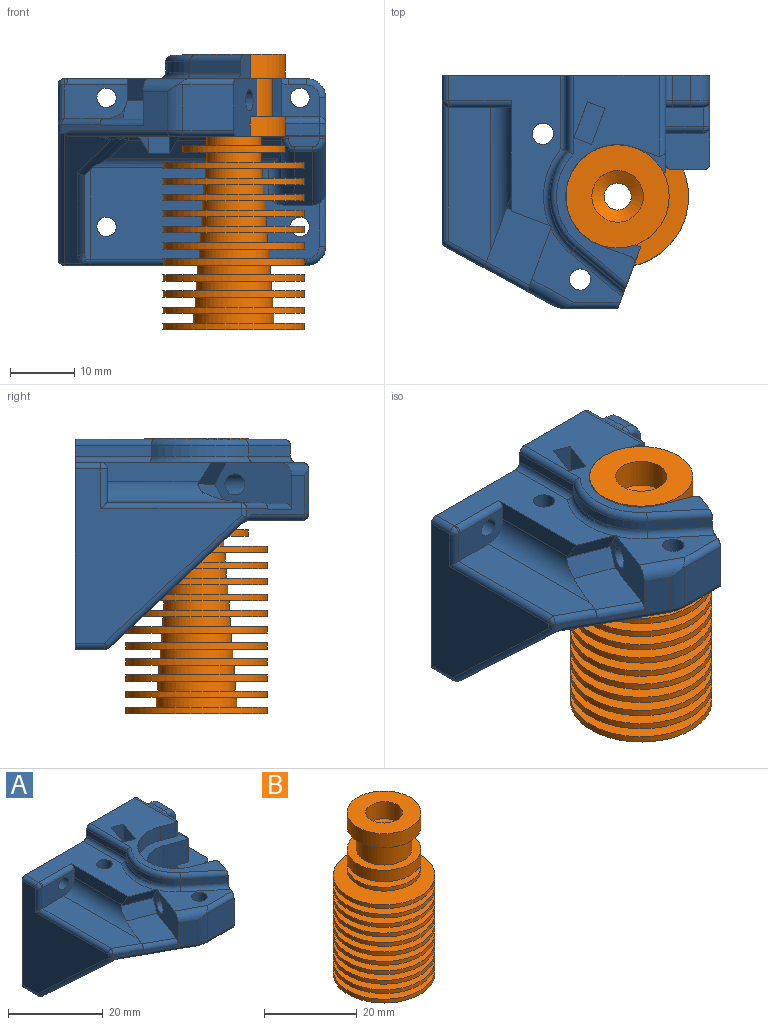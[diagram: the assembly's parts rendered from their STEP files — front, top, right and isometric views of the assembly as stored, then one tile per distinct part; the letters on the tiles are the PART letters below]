
ASSEMBLY  parts=2 mates=1
PART A: 143 faces, bbox 44.2x39.5x35.3 mm
  f0: plane 12.05x7.5mm, normal (-0.94,0.35,0), area 65.9mm2, adj f2,f6,f12,f24,f29,f71,f78,f128
  f1: plane 10.45x3.97mm, normal (0.94,-0.35,0), area 4.8mm2, adj f24,f78,f80,f121,f126,f128,f133
  f2: plane 7x4.48mm, normal (-0.3,-0.81,-0.5), area 27.6mm2, adj f0,f11,f71,f79,f80,f133
  f3: cylinder r=1mm len=12.2mm, axis (0,1,0), area 18.9mm2, adj f14,f15,f28,f72
  f4: cylinder r=1mm len=8.71mm, axis (-0.77,0.64,0), area 16.2mm2, adj f12,f71,f111,f112
  f5: cylinder r=1mm len=11.8mm, axis (0,-1,0), area 18.2mm2, adj f11,f14,f15,f71
  f6: cylinder r=2mm len=7.47mm, axis (0.88,-0.48,0), area 19.6mm2, adj f0,f7,f12,f24,f119
  f7: cylinder r=1mm len=8.72mm, axis (1,0,0), area 12.3mm2, adj f6,f12,f25,f26,f119
  f8: plane 5.92x5.33mm, normal (-0.35,-0.94,0), area 33.7mm2, adj f12,f27,f43,f114
  f9: plane 3.6x3.28mm, normal (-0.35,-0.94,0), area 12.6mm2, adj f12,f28,f98,f132
  f10: plane 5.92x5.74mm, normal (0.35,0.94,0), area 36.3mm2, adj f12,f26,f27,f114
  f11: plane 23.31x17.38mm, normal (0,0,1), area 178.3mm2, adj f2,f5,f14,f55,f56,f71,f79,f90
  f12: plane 24.46x20.78mm, normal (0,0,1), area 131.4mm2, adj f0,f4,f6,f7,f8,f9,f10,f26
  f13: plane 3.97x2.83mm, normal (0,0,1), area 11.2mm2, adj f14,f49,f68,f70
  f14: plane 41.5x32.61mm, normal (0,1,0), area 1226.5mm2, adj f3,f5,f11,f13,f15,f22,f23,f28
  f15: plane 11.8x1.6mm, normal (-1,0,0), area 18.9mm2, adj f3,f5,f14,f113
  f16: cylinder r=2mm len=6.18mm, axis (-0.58,0.58,-0.58), area 14mm2, adj f17,f63,f102,f103,f129,f131
  f17: sphere r=2mm, area 1.2mm2, adj f16,f18,f19
  f18: cylinder r=2mm len=2.07mm, axis (-1,0,0), area 2.9mm2, adj f17,f94,f95,f102,f137
  f19: cylinder r=2mm len=14.49mm, axis (0,-1,0), area 22.8mm2, adj f17,f20,f103,f137
  f20: bspline ~5.62x2.83mm, area 6.8mm2, adj f19,f39,f62,f137
  f21: plane 5.83x5.23mm, normal (0,-1,0), area 21.1mm2, adj f43,f47,f48,f49,f50,f82,f107
  f22: cylinder r=1.5mm len=4.97mm, axis (0,-1,0), area 46.9mm2, adj f14,f131
  f23: cylinder r=1.5mm len=4.97mm, axis (0,-1,0), area 46.9mm2, adj f14,f131
  f24: plane 16.48x9.06mm, normal (-0.48,-0.88,0), area 36.7mm2, adj f0,f1,f6,f39,f78,f119,f122,f123
  f25: plane 7.87x7mm, normal (0,-1,0), area 55.1mm2, adj f7,f26,f119,f142
  f26: plane 9.75x9.16mm, normal (0.94,-0.35,0), area 74mm2, adj f7,f10,f12,f25,f29,f99,f114,f137
  f27: cylinder r=6.05mm len=11.71mm, axis (0,0,1), area 112.5mm2, adj f8,f10,f12,f114
  f28: plane 32.38x15.96mm, normal (0,0,1), area 181.3mm2, adj f3,f9,f14,f72,f73,f98,f101,f104
  f29: cylinder r=1.65mm len=14.34mm, axis (0.94,-0.35,0), area 145.9mm2, adj f0,f26
  f30: cylinder r=2mm len=11.35mm, axis (0,0.75,-0.66), area 39.8mm2, adj f31,f40,f44,f74,f131
  f31: bspline ~2.09x2mm, area 3mm2, adj f30,f51,f52,f76
  f32: bspline ~2.09x2mm, area 3mm2, adj f33,f52,f66,f76
  f33: cylinder r=1mm len=1mm, axis (0,0,1), area 0.6mm2, adj f32,f75,f76,f77
  f34: cylinder r=1mm len=1.95mm, axis (0,0,-1), area 3.1mm2, adj f35,f40,f77,f81
  f35: sphere r=1mm, area 1mm2, adj f34,f36,f37
  f36: cylinder r=1mm len=4mm, axis (0,-1,0), area 5.5mm2, adj f35,f40,f47,f82
  f37: cylinder r=1mm len=5.83mm, axis (-1,0,0), area 9.2mm2, adj f35,f43,f81,f82
  f38: bspline ~2.04x1.4mm, area 2.2mm2, adj f39,f60,f127,f129
  f39: plane 22.71x21.32mm, normal (0,-0.68,-0.73), area 80.7mm2, adj f20,f24,f38,f59,f62,f122,f127,f137
  f40: plane 23.01x13.67mm, normal (1,0,0), area 144.3mm2, adj f14,f30,f34,f36,f44,f47,f51,f68
  f41: plane 37.5x4.58mm, normal (0,0,-1), area 150.8mm2, adj f14,f46,f57,f59,f61,f69
  f42: plane 27.01x25.74mm, normal (-1,0,0), area 350.5mm2, adj f14,f53,f56,f57,f122,f123,f124
  f43: plane 17.63x14mm, normal (1,0,0), area 84.9mm2, adj f8,f12,f14,f21,f37,f50,f70,f77
  f44: cylinder r=1mm len=8.17mm, axis (0,0,-1), area 11.7mm2, adj f30,f40,f45,f131
  f45: torus R=2mm, axis (0,-1,0), area 6.5mm2, adj f44,f46,f69,f131
  f46: cylinder r=1mm len=33.5mm, axis (-1,0,0), area 52.6mm2, adj f41,f45,f61,f131
  f47: cylinder r=1mm len=3.96mm, axis (0,0,-1), area 5.4mm2, adj f21,f36,f40,f48
  f48: torus R=2mm, axis (0,-1,0), area 6.5mm2, adj f21,f47,f49,f68
  f49: cylinder r=1mm len=2.83mm, axis (1,0,0), area 4.4mm2, adj f13,f21,f48,f50
  f50: torus R=2mm, axis (0,-1,0), area 2.1mm2, adj f21,f43,f49,f70
  f51: cylinder r=1mm len=1mm, axis (0,0,1), area 0.6mm2, adj f31,f40,f76,f77
  f52: cylinder r=1mm len=2.83mm, axis (-1,0,0), area 2.4mm2, adj f31,f32,f74,f76
  f53: cylinder r=1mm len=6.2mm, axis (0,0,1), area 9mm2, adj f42,f54,f120,f124
  f54: sphere r=1mm, area 2.1mm2, adj f53,f55,f56
  f55: cylinder r=1mm len=9.7mm, axis (1,0,0), area 15.2mm2, adj f11,f54,f79,f120
  f56: cylinder r=1mm len=3.97mm, axis (0,1,0), area 6.2mm2, adj f11,f14,f42,f54
  f57: cylinder r=1mm len=4.58mm, axis (0,1,0), area 7.2mm2, adj f14,f41,f42,f58
  f58: sphere r=1mm, area 0.8mm2, adj f57,f59,f122
  f59: cylinder r=1mm len=2.57mm, axis (1,0,0), area 1.9mm2, adj f39,f41,f58,f60
  f60: sphere r=1mm, area 0.2mm2, adj f38,f59,f61
  f61: torus R=2mm, axis (0,0,1), area 1.7mm2, adj f41,f46,f60,f129
  f62: cylinder r=2mm len=7.24mm, axis (0.56,-0.6,0.56), area 19.1mm2, adj f20,f39,f103,f127
  f63: cylinder r=2mm len=28.81mm, axis (-1,0,0), area 42mm2, adj f16,f64,f102,f131
  f64: cylinder r=2mm len=7.73mm, axis (0,0,-1), area 14.3mm2, adj f63,f67,f75,f102,f131
  f65: cylinder r=2mm len=16.25mm, axis (-1,0,0), area 25.2mm2, adj f75,f91,f92,f102,f137
  f66: cylinder r=2mm len=8.02mm, axis (0,-0.75,0.66), area 26.7mm2, adj f32,f67,f74,f75
  f67: bspline ~5.03x4.04mm, area 11.8mm2, adj f64,f66,f74,f131
  f68: cylinder r=3mm len=3.97mm, axis (0,1,0), area 18.7mm2, adj f13,f14,f40,f48
  f69: cylinder r=3mm len=3.97mm, axis (0,1,0), area 18.7mm2, adj f14,f40,f41,f45
  f70: cylinder r=1mm len=3.97mm, axis (0,1,0), area 6.2mm2, adj f13,f14,f43,f50
  f71: torus R=11.5mm, axis (0,0,-1), area 27mm2, adj f0,f2,f4,f5,f11,f12,f113
  f72: torus R=9.5mm, axis (0,0,1), area 25.9mm2, adj f3,f28,f73,f113
  f73: cylinder r=1mm len=8.44mm, axis (-0.77,0.64,0), area 15.7mm2, adj f28,f72,f111,f112
  f74: plane 9.36x8.27mm, normal (0,-0.66,-0.75), area 37.7mm2, adj f30,f52,f66,f67,f131
  f75: plane 6.7x6.28mm, normal (-1,0,0), area 19.8mm2, adj f33,f64,f65,f66,f77,f100,f102,f137
  f76: plane 4.83x1.69mm, normal (0,-1,0), area 7.6mm2, adj f31,f32,f33,f51,f52,f77
  f77: plane 6.83x6.7mm, normal (0,0,1), area 38.7mm2, adj f33,f34,f40,f43,f51,f75,f76,f81
  f78: cylinder r=1mm len=7.29mm, axis (-0.88,0.48,0), area 12mm2, adj f0,f1,f24,f128
  f79: plane 17.11x3mm, normal (-1,0,0), area 45.8mm2, adj f2,f11,f55,f80,f120
  f80: cylinder r=3.2mm len=22.24mm, axis (0,-1,0), area 84.9mm2, adj f1,f2,f79,f120,f121,f133
  f81: plane 5.83x1.95mm, normal (0,-1,0), area 11.4mm2, adj f34,f37,f43,f77
  f82: plane 5.83x3mm, normal (0,0,1), area 17.5mm2, adj f21,f36,f37,f43
  f83: plane 2.75x2mm, normal (0.87,0.5,0), area 6.4mm2, adj f84,f88,f89,f137
  f84: plane 3.18x2mm, normal (0,1,0), area 6.4mm2, adj f83,f85,f89,f137
  f85: plane 2.75x2mm, normal (-0.87,0.5,0), area 6.4mm2, adj f84,f86,f89,f137
  f86: plane 2.75x2mm, normal (-0.87,-0.5,0), area 6.4mm2, adj f85,f87,f89,f137
  f87: plane 3.18x2mm, normal (0,-1,0), area 6.4mm2, adj f86,f88,f89,f137
  f88: plane 2.75x2mm, normal (0.87,-0.5,0), area 6.4mm2, adj f83,f87,f89,f137
  f89: plane 6.35x5.5mm, normal (0,0,-1), area 17.6mm2, adj f83,f84,f85,f86,f87,f88,f118
  f90: cylinder r=1.65mm len=7mm, axis (0,0,1), area 72.6mm2, adj f11,f97
  f91: plane 2.76x2.13mm, normal (-0.87,0.5,0), area 6.4mm2, adj f65,f92,f96,f97,f137
  f92: plane 4.65x2.78mm, normal (-0.87,-0.5,0), area 10.4mm2, adj f65,f91,f93,f97,f102
  f93: plane 4.62x3.18mm, normal (0,-1,0), area 14.7mm2, adj f92,f94,f97,f102
  f94: plane 4.65x2.78mm, normal (0.87,-0.5,0), area 10.4mm2, adj f18,f93,f95,f97,f102
  f95: plane 2.76x2.13mm, normal (0.87,0.5,0), area 6.4mm2, adj f18,f94,f96,f97,f137
  f96: plane 3.18x2mm, normal (0,1,0), area 6.4mm2, adj f91,f95,f97,f137
  f97: plane 6.35x5.5mm, normal (0,0,-1), area 17.6mm2, adj f90,f91,f92,f93,f94,f95,f96
  f98: cylinder r=1mm len=3.6mm, axis (0,0,-1), area 6.4mm2, adj f9,f12,f28,f43,f138
  f99: cylinder r=1mm len=3.08mm, axis (0,0,1), area 4.8mm2, adj f26,f114,f115,f137
  f100: cylinder r=1mm len=3.08mm, axis (0,0,-1), area 5.9mm2, adj f43,f75,f114,f116,f137
  f101: cylinder r=1mm len=3.6mm, axis (0,0,-1), area 5.7mm2, adj f12,f28,f110,f111
  f102: plane 26.79x2.95mm, normal (0,-0.71,-0.71), area 88.1mm2, adj f16,f18,f63,f64,f65,f75,f92,f93
  f103: plane 19.55x5.71mm, normal (0.71,0,-0.71), area 109mm2, adj f16,f19,f62,f127,f129,f130
  f104: plane 10.62x5.59mm, normal (0.94,-0.35,0), area 54.9mm2, adj f28,f105,f109,f135,f136
  f105: plane 10.62x2.71mm, normal (-0.35,-0.94,0), area 30.8mm2, adj f28,f104,f134,f136
  f106: cylinder r=1.5mm len=4.97mm, axis (0,-1,0), area 46.9mm2, adj f14,f120
  f107: cylinder r=1.5mm len=4.97mm, axis (0,-1,0), area 46.9mm2, adj f14,f21
  f108: plane 3.3x3.09mm, normal (0.94,-0.35,0), area 8.6mm2, adj f109
  f109: cylinder r=1.65mm len=8.32mm, axis (0.94,-0.35,0), area 79.3mm2, adj f104,f108
  f110: plane 4.8x3.6mm, normal (0.35,0.94,0), area 18.5mm2, adj f12,f28,f101,f132
  f111: plane 5.08x3.75mm, normal (0.94,-0.35,0), area 15.2mm2, adj f4,f12,f28,f73,f101,f112
  f112: plane 7.8x6.51mm, normal (-0.64,-0.77,0), area 16.3mm2, adj f4,f73,f111,f113
  f113: cylinder r=10.5mm len=15.06mm, axis (0,0,-1), area 27mm2, adj f15,f71,f72,f112
  f114: plane 18.68x15.51mm, normal (0,0,-1), area 67.9mm2, adj f8,f10,f26,f27,f43,f99,f100,f115
  f115: plane 4.8x3.08mm, normal (0.35,0.94,0), area 15.8mm2, adj f99,f114,f117,f137
  f116: plane 3.28x3.08mm, normal (-0.35,-0.94,0), area 10.8mm2, adj f100,f114,f117,f137
  f117: cylinder r=8.05mm len=15.59mm, axis (0,0,1), area 77.9mm2, adj f114,f115,f116,f137
  f118: cylinder r=1.65mm len=7mm, axis (0,0,1), area 72.6mm2, adj f12,f89
  f119: cylinder r=5mm len=7.21mm, axis (0,0,-1), area 16.8mm2, adj f6,f7,f24,f25,f141
  f120: plane 9.7x5.2mm, normal (0,-1,0), area 41.2mm2, adj f53,f55,f79,f80,f106,f121
  f121: plane 23.97x6.5mm, normal (0,0,1), area 145.9mm2, adj f1,f80,f120,f124,f126
  f122: cylinder r=1mm len=22.3mm, axis (0,-0.73,0.68), area 46mm2, adj f24,f39,f42,f58,f123
  f123: cylinder r=1mm len=1.36mm, axis (0,0,-1), area 1.3mm2, adj f24,f42,f122,f125
  f124: cylinder r=1mm len=21.77mm, axis (0,1,0), area 33.4mm2, adj f42,f53,f121,f125
  f125: sphere r=1mm, area 0.8mm2, adj f123,f124,f126
  f126: cylinder r=1mm len=6.45mm, axis (-0.88,0.48,0), area 10.6mm2, adj f1,f24,f121,f125
  f127: cylinder r=1mm len=14.35mm, axis (0,0.73,-0.68), area 28.1mm2, adj f38,f39,f62,f103,f130
  f128: plane 12.03x10.21mm, normal (0,0,1), area 71.5mm2, adj f0,f1,f78,f133
  f129: cylinder r=1mm len=13.98mm, axis (0,0,1), area 20.6mm2, adj f16,f38,f61,f103,f130,f131
  f130: plane 12.49x11.71mm, normal (1,0,0), area 73.1mm2, adj f103,f127,f129
  f131: plane 35.87x14.56mm, normal (0,-1,0), area 443.8mm2, adj f16,f22,f23,f30,f44,f45,f46,f63
  f132: cylinder r=8.05mm len=15.59mm, axis (0,0,-1), area 91mm2, adj f9,f12,f28,f110
  f133: plane 7.71x4.27mm, normal (-0.3,-0.81,0.5), area 25.8mm2, adj f0,f1,f2,f80,f128
  f134: plane 10.62x5.59mm, normal (-0.94,0.35,0), area 54.9mm2, adj f28,f105,f135,f136,f139
  f135: plane 10.62x2.71mm, normal (0.35,0.94,0), area 30.8mm2, adj f28,f104,f134,f136
  f136: plane 6.61x4.82mm, normal (0,0,1), area 17.3mm2, adj f104,f105,f134,f135
  f137: plane 32.59x25.42mm, normal (0,0,-1), area 308.1mm2, adj f18,f19,f20,f26,f39,f65,f75,f83
  f138: cylinder r=1mm len=12.57mm, axis (0,-1,0), area 19mm2, adj f14,f28,f43,f98
  f139: cylinder r=1.65mm len=12.22mm, axis (0.94,-0.35,0), area 122.5mm2, adj f43,f134
  f140: cylinder r=1mm len=16.39mm, axis (0.88,-0.48,0), area 28mm2, adj f24,f39,f137,f141
  f141: torus R=4mm, axis (0,0,1), area 3.6mm2, adj f119,f137,f140,f142
  f142: cylinder r=1mm len=8.25mm, axis (1,0,0), area 12.7mm2, adj f25,f26,f137,f141
PART B: 62 faces, bbox 22x22x42.7 mm
  f0: cylinder r=3mm len=6mm, axis (0,0,-1), area 95mm2, adj f59,f60
  f1: cylinder r=2.1mm len=21.42mm, axis (0,0,1), area 282.6mm2, adj f57,f59
  f2: plane 22x22mm, normal (0,0,1), area 272.6mm2, adj f3,f56
  f3: cylinder r=5.85mm len=11.7mm, axis (0,0,1), area 55.1mm2, adj f2,f4
  f4: plane 22x22mm, normal (0,0,-1), area 272.6mm2, adj f3,f5
  f5: cylinder r=11mm len=22mm, axis (0,0,1), area 69.1mm2, adj f4,f6
  f6: plane 22x22mm, normal (0,0,1), area 279.8mm2, adj f5,f7
  f7: cylinder r=5.65mm len=11.3mm, axis (0,0,1), area 53.2mm2, adj f6,f8
  f8: plane 22x22mm, normal (0,0,-1), area 279.8mm2, adj f7,f9
  f9: cylinder r=11mm len=22mm, axis (0,0,1), area 69.1mm2, adj f8,f10
  f10: plane 22x22mm, normal (0,0,1), area 286.8mm2, adj f9,f11
  f11: cylinder r=5.45mm len=10.9mm, axis (0,0,1), area 51.4mm2, adj f10,f12
  f12: plane 22x22mm, normal (0,0,-1), area 286.8mm2, adj f11,f13
  f13: cylinder r=11mm len=22mm, axis (0,0,1), area 69.1mm2, adj f12,f14
  f14: plane 22x22mm, normal (0,0,1), area 293.5mm2, adj f13,f15
  f15: cylinder r=5.25mm len=10.5mm, axis (0,0,1), area 49.5mm2, adj f14,f16
  f16: plane 22x22mm, normal (0,0,-1), area 293.5mm2, adj f15,f17
  f17: cylinder r=11mm len=22mm, axis (0,0,1), area 69.1mm2, adj f16,f18
  f18: plane 22x22mm, normal (0,0,1), area 300mm2, adj f17,f19
  f19: cylinder r=5.05mm len=10.1mm, axis (0,0,1), area 47.6mm2, adj f18,f20
  f20: plane 22x22mm, normal (0,0,-1), area 300mm2, adj f19,f21
  f21: cylinder r=11mm len=22mm, axis (0,0,1), area 69.1mm2, adj f20,f22
  f22: plane 22x22mm, normal (0,0,1), area 306.2mm2, adj f21,f23
  f23: cylinder r=4.85mm len=9.7mm, axis (0,0,1), area 45.7mm2, adj f22,f24
  f24: plane 22x22mm, normal (0,0,-1), area 306.2mm2, adj f23,f25
  f25: cylinder r=11mm len=22mm, axis (0,0,1), area 69.1mm2, adj f24,f26
  f26: plane 22x22mm, normal (0,0,1), area 312.2mm2, adj f25,f27
  f27: cylinder r=4.65mm len=9.3mm, axis (0,0,1), area 43.8mm2, adj f26,f28
  f28: plane 22x22mm, normal (0,0,-1), area 312.2mm2, adj f27,f29
  f29: cylinder r=11mm len=22mm, axis (0,0,1), area 69.1mm2, adj f28,f30
  f30: plane 22x22mm, normal (0,0,1), area 317.9mm2, adj f29,f31
  f31: cylinder r=4.45mm len=8.9mm, axis (0,0,1), area 41.9mm2, adj f30,f32
  f32: plane 22x22mm, normal (0,0,-1), area 317.9mm2, adj f31,f33
  f33: cylinder r=11mm len=22mm, axis (0,0,1), area 69.1mm2, adj f32,f34
  f34: plane 22x22mm, normal (0,0,1), area 323.4mm2, adj f33,f35
  f35: cylinder r=4.25mm len=8.5mm, axis (0,0,1), area 40.1mm2, adj f34,f36
  f36: plane 16x16mm, normal (0,0,-1), area 144.3mm2, adj f35,f37
  f37: cylinder r=8mm len=16mm, axis (0,0,1), area 50.3mm2, adj f36,f38
  f38: plane 16x16mm, normal (0,0,1), area 144.3mm2, adj f37,f39
  f39: cylinder r=4.25mm len=8.5mm, axis (0,0,1), area 40.1mm2, adj f38,f40
  f40: plane 16x16mm, normal (0,0,-1), area 144.3mm2, adj f39,f41
  f41: cylinder r=8mm len=16mm, axis (0,0,1), area 150.8mm2, adj f40,f42
  f42: plane 16x16mm, normal (0,0,1), area 88mm2, adj f41,f43
  f43: cylinder r=6mm len=12mm, axis (0,0,1), area 226.2mm2, adj f42,f44
  f44: plane 16x16mm, normal (0,0,-1), area 88mm2, adj f43,f45
  f45: cylinder r=8mm len=16mm, axis (0,0,1), area 186mm2, adj f44,f46
  f46: plane 16x16mm, normal (0,0,1), area 150.8mm2, adj f45,f58
  f47: plane 22x22mm, normal (0,0,-1), area 349.9mm2, adj f48,f61
  f48: cylinder r=11mm len=22mm, axis (0,0,1), area 69.1mm2, adj f47,f49
  f49: plane 22x22mm, normal (0,0,1), area 257.4mm2, adj f48,f50
  f50: cylinder r=6.25mm len=12.5mm, axis (0,0,1), area 58.9mm2, adj f49,f51
  f51: plane 22x22mm, normal (0,0,-1), area 257.4mm2, adj f50,f52
  f52: cylinder r=11mm len=22mm, axis (0,0,1), area 69.1mm2, adj f51,f53
  f53: plane 22x22mm, normal (0,0,1), area 265.1mm2, adj f52,f54
  f54: cylinder r=6.05mm len=12.1mm, axis (0,0,1), area 57mm2, adj f53,f55
  f55: plane 22x22mm, normal (0,0,-1), area 265.1mm2, adj f54,f56
  f56: cylinder r=11mm len=22mm, axis (0,0,1), area 69.1mm2, adj f2,f55
  f57: cone r=0mm half-angle=59deg, axis (0,0,1), area 42.5mm2, adj f1,f58
  f58: cylinder r=4mm len=8mm, axis (0,0,1), area 113.1mm2, adj f46,f57
  f59: cone r=0mm half-angle=59deg, axis (0,0,-1), area 16.8mm2, adj f0,f1
  f60: cone r=0mm half-angle=59deg, axis (0,0,-1), area 2.2mm2, adj f0,f61
  f61: cylinder r=3.1mm len=10mm, axis (0,0,-1), area 194.8mm2, adj f47,f60
PLACE A t=(22.9,-55.79,0.71)mm fixed
PLACE B t=(-75.58,-7,38.7)mm
MATE fastened B.f0 <-> A.f27  axis (0,0,1) through (-75.58,-7,32)mm
